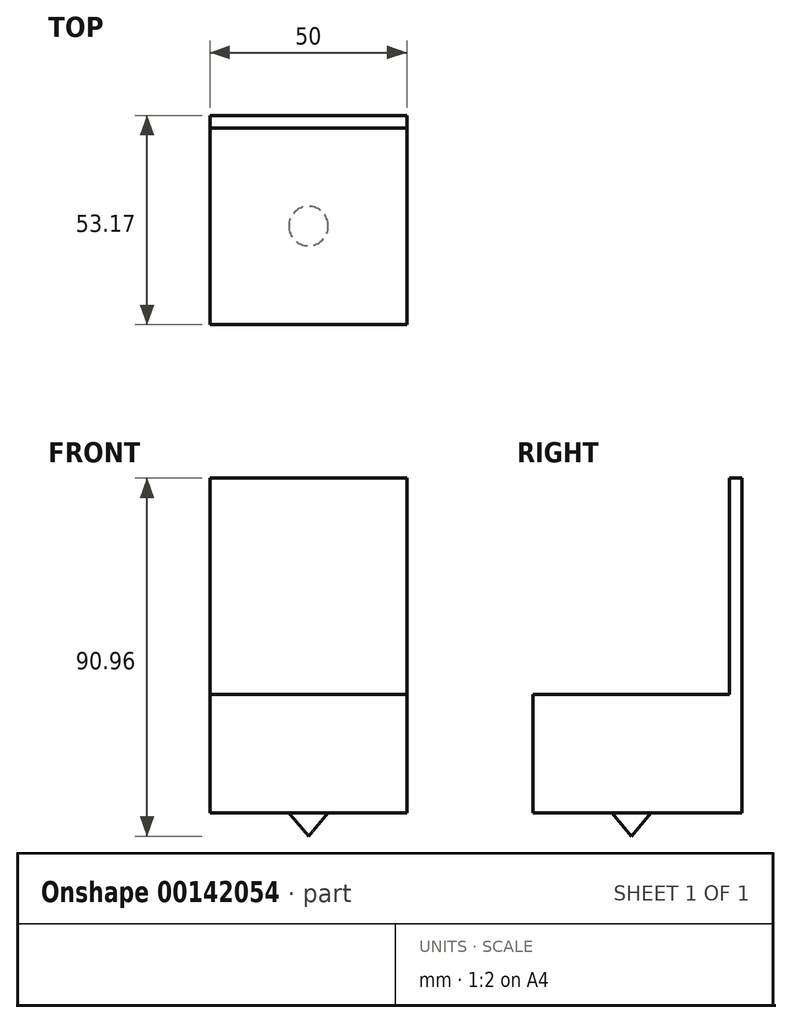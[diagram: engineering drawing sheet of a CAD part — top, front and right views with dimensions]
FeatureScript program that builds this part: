
annotation { "Feature Type Name" : "Feature", "Feature Type Description" : "" }
export const myFeature = defineFeature(function(context is Context, id is Id, definition is map)
    precondition{}
    {
        {
            var Q0;
            Q0=qCreatedBy(makeId("Top.planeOp"),FACE);
            var sketch = newSketch(context, id + "F0", { "sketchPlane" : qUnion([Q0])});
            skLineSegment(sketch, "E0.bottom", {"start": v(-45.76, 10.4) * mm, "end": v(4.24, 10.4) * mm});
            skLineSegment(sketch, "E0.top", {"start": v(-45.76, -39.6) * mm, "end": v(4.24, -39.6) * mm});
            skLineSegment(sketch, "E0.left", {"start": v(-45.76, 10.4) * mm, "end": v(-45.76, -39.6) * mm});
            skLineSegment(sketch, "E0.right", {"start": v(4.24, 10.4) * mm, "end": v(4.24, -39.6) * mm});
            skSolve(sketch);
        }
        {
            var Q0;
            Q0 = qSketchRegion(id + "F0", true);
            extrude(context, id + "F1", {"entities" : qUnion([Q0]), "depth" : 30 * mm});
        }
        {
            var Q0;
            Q0=makeQuery(id+"F1.opExtrude","SWEPT_FACE",FACE,{"disambiguationData":[OSD([sQuery(id+"F0.wireOp",EDGE,"E0.bottom")])]});
            var sketch = newSketch(context, id + "F2", { "sketchPlane" : qUnion([Q0])});
            skLineSegment(sketch, "E1.bottom", {"start": v(-4.24, 0) * mm, "end": v(45.76, 0) * mm});
            skLineSegment(sketch, "E1.top", {"start": v(-4.24, 85) * mm, "end": v(45.76, 85) * mm});
            skLineSegment(sketch, "E1.left", {"start": v(-4.24, 0) * mm, "end": v(-4.24, 85) * mm});
            skLineSegment(sketch, "E1.right", {"start": v(45.76, 0) * mm, "end": v(45.76, 85) * mm});
            skLineSegment(sketch, "E2.0.1", {"start": v(45.76, 0) * mm, "end": v(45.76, 30) * mm});
            skLineSegment(sketch, "E2.0.2", {"start": v(45.76, 30) * mm, "end": v(-4.24, 30) * mm});
            skLineSegment(sketch, "E2.0.3", {"start": v(-4.24, 30) * mm, "end": v(-4.24, 0) * mm});
            skSolve(sketch);
        }
        {
            var Q0;
            Q0 = qSketchRegion(id + "F2", true);
            extrude(context, id + "F3", {"entities" : qUnion([Q0]), "operationType" : NewBodyOperationType.ADD, "depth" : 3.17 * mm});
        }
        {
            var Q0;
            Q0=makeQuery(id+"F3.boolean.opBoolean","MERGE",FACE,{"derivedFrom":[makeQuery(id+"F1.opExtrude","CAP_FACE",FACE,{"disambiguationData":[OSD([sQuery(id+"F0.wireOp",EDGE,"E0.bottom"),sQuery(id+"F0.wireOp",EDGE,"E0.top"),sQuery(id+"F0.wireOp",EDGE,"E0.left"),sQuery(id+"F0.wireOp",EDGE,"E0.right")])],"isStart":true}),makeQuery(id+"F3.opExtrude","SWEPT_FACE",FACE,{"disambiguationData":[OSD([sQuery(id+"F2.wireOp",EDGE,"E1.bottom")])]})]});
            var sketch = newSketch(context, id + "F4", { "sketchPlane" : qUnion([Q0])});
            skLineSegment(sketch, "E3.0.0", {"start": v(-45.76, 39.6) * mm, "end": v(-45.76, -13.58) * mm});
            skLineSegment(sketch, "E3.0.1", {"start": v(-45.76, -13.58) * mm, "end": v(4.24, -13.58) * mm});
            skLineSegment(sketch, "E3.0.2", {"start": v(4.24, -13.58) * mm, "end": v(4.24, 39.6) * mm});
            skLineSegment(sketch, "E3.0.3", {"start": v(4.24, 39.6) * mm, "end": v(-45.76, 39.6) * mm});
            skCircle(sketch, "E4", {"center": v(-20.76, 14.54) * mm, "radius": 25.05 * mm});
            skPoint(sketch, "E4.first.point", {"position": v(-45.76, 13) * mm});
            skPoint(sketch, "E4.second.point", {"position": v(-20.76, 39.6) * mm});
            skPoint(sketch, "E4.third.point", {"position": v(4.24, 13) * mm});
            skCircle(sketch, "E5", {"center": v(-20.76, 14.54) * mm, "radius": 5 * mm});
            skSolve(sketch);
        }
        {
            var Q0;
            Q0=makeQuery(id+"F4.imprint","IMPRINT",FACE,{"disambiguationData":[TD([[makeQuery(id+"F4.imprint","IMPRINT",EDGE,{"derivedFrom":sQuery(id+"F4.wireOp",EDGE,"E5")}),1.0]])]});
            extrude(context, id + "F5", {"entities" : qUnion([Q0]), "operationType" : NewBodyOperationType.ADD, "depth" : 25.4 * mm, "hasDraft" : true, "draftAngle" : 40 * degree, "draftPullDirection" : true});
        }
    });
